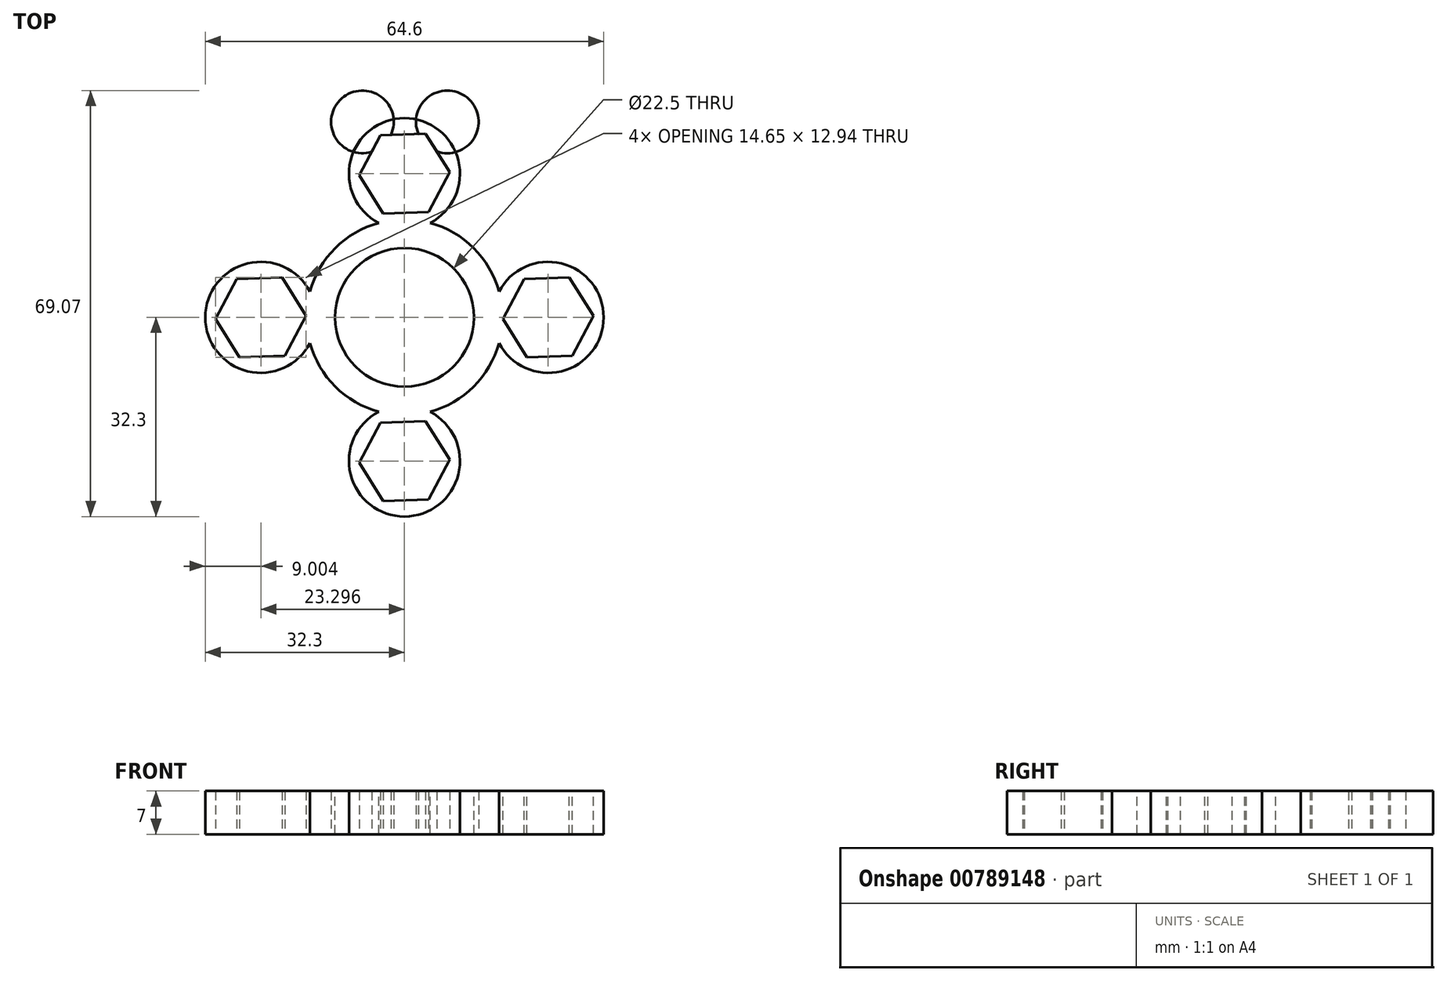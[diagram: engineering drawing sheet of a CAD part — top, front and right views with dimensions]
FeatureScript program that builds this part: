
annotation { "Feature Type Name" : "Feature", "Feature Type Description" : "" }
export const myFeature = defineFeature(function(context is Context, id is Id, definition is map)
    precondition{}
    {
        {
            var Q0;
            Q0=qCreatedBy(makeId("Top.planeOp"),FACE);
            var sketch = newSketch(context, id + "F0", { "sketchPlane" : qUnion([Q0])});
            skCircle(sketch, "E0", {"center": v(0, 0) * mm, "radius": 11.25 * mm});
            skSolve(sketch);
        }
        {
            var Q0;
            Q0=makeQuery(id+"F0.imprint","IMPRINT",FACE,{"disambiguationData":[TD([[makeQuery(id+"F0.imprint","IMPRINT",EDGE,{"derivedFrom":sQuery(id+"F0.wireOp",EDGE,"E0")}),1.0]])]});
            var sketch = newSketch(context, id + "F1", { "sketchPlane" : qUnion([Q0])});
            skCircle(sketch, "E1", {"center": v(0, 0) * mm, "radius": 14.3 * mm});
            skSolve(sketch);
        }
        {
            var Q0;
            Q0=makeQuery(id+"F0.imprint","IMPRINT",FACE,{"disambiguationData":[TD([[makeQuery(id+"F0.imprint","IMPRINT",EDGE,{"derivedFrom":sQuery(id+"F0.wireOp",EDGE,"E0")}),1.0]])]});
            var sketch = newSketch(context, id + "F2", { "sketchPlane" : qUnion([Q0])});
            skLineSegment(sketch, "E2", {"start": v(0, 0) * mm, "end": v(0, 55.77) * mm});
            skLineSegment(sketch, "E3", {"start": v(0, 55.77) * mm, "end": v(0, -44.4) * mm});
            skSolve(sketch);
        }
        {
            var Q0;
            Q0=makeQuery(id+"F0.imprint","IMPRINT",FACE,{"disambiguationData":[TD([[makeQuery(id+"F0.imprint","IMPRINT",EDGE,{"derivedFrom":sQuery(id+"F0.wireOp",EDGE,"E0")}),1.0]])]});
            var sketch = newSketch(context, id + "F3", { "sketchPlane" : qUnion([Q0])});
            skLineSegment(sketch, "E4", {"start": v(0, 0) * mm, "end": v(-73.88, 0) * mm});
            skLineSegment(sketch, "E5", {"start": v(-73.88, 0) * mm, "end": v(73.58, 0) * mm});
            skSolve(sketch);
        }
        {
            var Q0;
            Q0=makeQuery(id+"F0.imprint","IMPRINT",FACE,{"disambiguationData":[TD([[makeQuery(id+"F0.imprint","IMPRINT",EDGE,{"derivedFrom":sQuery(id+"F0.wireOp",EDGE,"E0")}),1.0]])]});
            var sketch = newSketch(context, id + "F4", { "sketchPlane" : qUnion([Q0])});
            skCircle(sketch, "E6", {"center": v(0, 23.3) * mm, "radius": 9 * mm});
            skSolve(sketch);
        }
        {
            var Q0;
            Q0=makeQuery(id+"F0.imprint","IMPRINT",FACE,{"disambiguationData":[TD([[makeQuery(id+"F0.imprint","IMPRINT",EDGE,{"derivedFrom":sQuery(id+"F0.wireOp",EDGE,"E0")}),1.0]])]});
            var sketch = newSketch(context, id + "F5", { "sketchPlane" : qUnion([Q0])});
            skCircle(sketch, "E7", {"center": v(-23.3, 0) * mm, "radius": 9 * mm});
            skSolve(sketch);
        }
        {
            var Q0;
            Q0=makeQuery(id+"F0.imprint","IMPRINT",FACE,{"disambiguationData":[TD([[makeQuery(id+"F0.imprint","IMPRINT",EDGE,{"derivedFrom":sQuery(id+"F0.wireOp",EDGE,"E0")}),1.0]])]});
            var sketch = newSketch(context, id + "F6", { "sketchPlane" : qUnion([Q0])});
            skCircle(sketch, "E8", {"center": v(0, -23.3) * mm, "radius": 9 * mm});
            skSolve(sketch);
        }
        {
            var Q0;
            Q0=makeQuery(id+"F0.imprint","IMPRINT",FACE,{"disambiguationData":[TD([[makeQuery(id+"F0.imprint","IMPRINT",EDGE,{"derivedFrom":sQuery(id+"F0.wireOp",EDGE,"E0")}),1.0]])]});
            var sketch = newSketch(context, id + "F7", { "sketchPlane" : qUnion([Q0])});
            skCircle(sketch, "E9", {"center": v(23.3, 0) * mm, "radius": 9 * mm});
            skSolve(sketch);
        }
        {
            var Q0;
            Q0=makeQuery(id+"F0.imprint","IMPRINT",FACE,{"disambiguationData":[TD([[makeQuery(id+"F0.imprint","IMPRINT",EDGE,{"derivedFrom":sQuery(id+"F0.wireOp",EDGE,"E0")}),1.0]])]});
            var sketch = newSketch(context, id + "F8", { "sketchPlane" : qUnion([Q0])});
            skCircle(sketch, "E10.cCircle", {"center": v(23.3, 0) * mm, "radius": 7.33 * mm, "construction": true});
            skLineSegment(sketch, "E10.0", {"start": v(26.73, 6.47) * mm, "end": v(30.62, 0.26) * mm});
            skLineSegment(sketch, "E10.1", {"start": v(30.62, 0.26) * mm, "end": v(27.18, -6.21) * mm});
            skLineSegment(sketch, "E10.2", {"start": v(27.18, -6.21) * mm, "end": v(19.86, -6.47) * mm});
            skLineSegment(sketch, "E10.3", {"start": v(19.86, -6.47) * mm, "end": v(15.97, -0.26) * mm});
            skLineSegment(sketch, "E10.4", {"start": v(15.97, -0.26) * mm, "end": v(19.4, 6.21) * mm});
            skLineSegment(sketch, "E10.5", {"start": v(19.4, 6.21) * mm, "end": v(26.73, 6.47) * mm});
            skSolve(sketch);
        }
        {
            var Q0;
            Q0=makeQuery(id+"F8.imprint","IMPRINT",FACE,{"disambiguationData":[TD([[makeQuery(id+"F8.imprint","IMPRINT",EDGE,{"derivedFrom":sQuery(id+"F8.wireOp",EDGE,"E10.0")}),-1.0]])]});
            var sketch = newSketch(context, id + "F9", { "sketchPlane" : qUnion([Q0])});
            skCircle(sketch, "E11.cCircle", {"center": v(0, -23.3) * mm, "radius": 7.33 * mm, "construction": true});
            skLineSegment(sketch, "E11.0", {"start": v(3.44, -16.82) * mm, "end": v(7.32, -23.04) * mm});
            skLineSegment(sketch, "E11.1", {"start": v(7.32, -23.04) * mm, "end": v(3.89, -29.5) * mm});
            skLineSegment(sketch, "E11.2", {"start": v(3.89, -29.5) * mm, "end": v(-3.44, -29.77) * mm});
            skLineSegment(sketch, "E11.3", {"start": v(-3.44, -29.77) * mm, "end": v(-7.32, -23.56) * mm});
            skLineSegment(sketch, "E11.4", {"start": v(-7.32, -23.56) * mm, "end": v(-3.89, -17.08) * mm});
            skLineSegment(sketch, "E11.5", {"start": v(-3.89, -17.08) * mm, "end": v(3.44, -16.82) * mm});
            skSolve(sketch);
        }
        {
            var Q0;
            Q0=makeQuery(id+"F5.imprint","IMPRINT",FACE,{"disambiguationData":[TD([[makeQuery(id+"F5.imprint","IMPRINT",EDGE,{"derivedFrom":sQuery(id+"F5.wireOp",EDGE,"E7")}),1.0]])]});
            var sketch = newSketch(context, id + "F10", { "sketchPlane" : qUnion([Q0])});
            skCircle(sketch, "E12.cCircle", {"center": v(-23.3, 0) * mm, "radius": 7.33 * mm, "construction": true});
            skLineSegment(sketch, "E12.0", {"start": v(-19.86, 6.47) * mm, "end": v(-15.97, 0.26) * mm});
            skLineSegment(sketch, "E12.1", {"start": v(-15.97, 0.26) * mm, "end": v(-19.4, -6.21) * mm});
            skLineSegment(sketch, "E12.2", {"start": v(-19.4, -6.21) * mm, "end": v(-26.73, -6.47) * mm});
            skLineSegment(sketch, "E12.3", {"start": v(-26.73, -6.47) * mm, "end": v(-30.62, -0.26) * mm});
            skLineSegment(sketch, "E12.4", {"start": v(-30.62, -0.26) * mm, "end": v(-27.18, 6.21) * mm});
            skLineSegment(sketch, "E12.5", {"start": v(-27.18, 6.21) * mm, "end": v(-19.86, 6.47) * mm});
            skSolve(sketch);
        }
        {
            var Q0;
            Q0=makeQuery(id+"F4.imprint","IMPRINT",FACE,{"disambiguationData":[TD([[makeQuery(id+"F4.imprint","IMPRINT",EDGE,{"derivedFrom":sQuery(id+"F4.wireOp",EDGE,"E6")}),1.0]])]});
            var sketch = newSketch(context, id + "F11", { "sketchPlane" : qUnion([Q0])});
            skCircle(sketch, "E13.cCircle", {"center": v(0, 23.3) * mm, "radius": 7.33 * mm, "construction": true});
            skLineSegment(sketch, "E13.0", {"start": v(3.44, 29.77) * mm, "end": v(7.32, 23.56) * mm});
            skLineSegment(sketch, "E13.1", {"start": v(7.32, 23.56) * mm, "end": v(3.89, 17.08) * mm});
            skLineSegment(sketch, "E13.2", {"start": v(3.89, 17.08) * mm, "end": v(-3.44, 16.82) * mm});
            skLineSegment(sketch, "E13.3", {"start": v(-3.44, 16.82) * mm, "end": v(-7.32, 23.04) * mm});
            skLineSegment(sketch, "E13.4", {"start": v(-7.32, 23.04) * mm, "end": v(-3.89, 29.5) * mm});
            skLineSegment(sketch, "E13.5", {"start": v(-3.89, 29.5) * mm, "end": v(3.44, 29.77) * mm});
            skSolve(sketch);
        }
        {
            var Q0;
            Q0=makeQuery(id+"F4.imprint","IMPRINT",FACE,{"disambiguationData":[TD([[makeQuery(id+"F4.imprint","IMPRINT",EDGE,{"derivedFrom":sQuery(id+"F4.wireOp",EDGE,"E6")}),1.0]])]});
            var sketch = newSketch(context, id + "F12", { "sketchPlane" : qUnion([Q0])});
            skCircle(sketch, "E14", {"center": v(-6.82, 31.69) * mm, "radius": 5.08 * mm});
            skCircle(sketch, "E15", {"center": v(6.94, 31.69) * mm, "radius": 5.08 * mm});
            skSolve(sketch);
        }
        {
            var Q0;
            Q0=makeQuery(id+"F1.imprint","IMPRINT",FACE,{"disambiguationData":[TD([[makeQuery(id+"F1.imprint","IMPRINT",EDGE,{"derivedFrom":makeQuery(id+"F0.imprint","IMPRINT",EDGE,{"derivedFrom":sQuery(id+"F0.wireOp",EDGE,"E0")})}),1.0]])]});
            var Q1;
            Q1=makeQuery(id+"F1.imprint","IMPRINT",FACE,{"disambiguationData":[TD([[makeQuery(id+"F1.imprint","IMPRINT",EDGE,{"derivedFrom":sQuery(id+"F1.wireOp",EDGE,"E1")}),1.0]])]});
            var Q2;
            {var subQ0=sQuery(id+"F2.wireOp",EDGE,"E3");var subQ1=makeQuery(id+"F2.imprint","IMPRINT",VERTEX,{"derivedFrom":subQ0});Q2=makeQuery(id+"F2.imprint","IMPRINT",FACE,{"disambiguationData":[TD([[makeQuery(id+"F2.imprint","IMPRINT",EDGE,{"disambiguationData":[TD([[subQ1,1.0]])],"derivedFrom":subQ0}),-1.0]])]});}
            var Q3;
            {var subQ0=sQuery(id+"F2.wireOp",EDGE,"E3");var subQ1=makeQuery(id+"F2.imprint","IMPRINT",VERTEX,{"derivedFrom":subQ0});Q3=makeQuery(id+"F2.imprint","IMPRINT",FACE,{"disambiguationData":[TD([[makeQuery(id+"F2.imprint","IMPRINT",EDGE,{"disambiguationData":[TD([[subQ1,1.0]])],"derivedFrom":subQ0}),1.0]])]});}
            var Q4;
            {var subQ0=sQuery(id+"F3.wireOp",EDGE,"E5");var subQ1=makeQuery(id+"F3.imprint","IMPRINT",VERTEX,{"derivedFrom":subQ0});Q4=makeQuery(id+"F3.imprint","IMPRINT",FACE,{"disambiguationData":[TD([[makeQuery(id+"F3.imprint","IMPRINT",EDGE,{"disambiguationData":[TD([[subQ1,1.0]])],"derivedFrom":subQ0}),-1.0]])]});}
            var Q5;
            {var subQ0=sQuery(id+"F3.wireOp",EDGE,"E5");var subQ1=makeQuery(id+"F3.imprint","IMPRINT",VERTEX,{"derivedFrom":subQ0});Q5=makeQuery(id+"F3.imprint","IMPRINT",FACE,{"disambiguationData":[TD([[makeQuery(id+"F3.imprint","IMPRINT",EDGE,{"disambiguationData":[TD([[subQ1,1.0]])],"derivedFrom":subQ0}),1.0]])]});}
            var Q6;
            Q6=makeQuery(id+"F4.imprint","IMPRINT",FACE,{"disambiguationData":[TD([[makeQuery(id+"F4.imprint","IMPRINT",EDGE,{"derivedFrom":sQuery(id+"F4.wireOp",EDGE,"E6")}),1.0]])]});
            var Q7;
            Q7=makeQuery(id+"F7.imprint","IMPRINT",FACE,{"disambiguationData":[TD([[makeQuery(id+"F7.imprint","IMPRINT",EDGE,{"derivedFrom":sQuery(id+"F7.wireOp",EDGE,"E9")}),1.0]])]});
            var Q8;
            Q8=makeQuery(id+"F6.imprint","IMPRINT",FACE,{"disambiguationData":[TD([[makeQuery(id+"F6.imprint","IMPRINT",EDGE,{"derivedFrom":sQuery(id+"F6.wireOp",EDGE,"E8")}),1.0]])]});
            var Q9;
            Q9=makeQuery(id+"F5.imprint","IMPRINT",FACE,{"disambiguationData":[TD([[makeQuery(id+"F5.imprint","IMPRINT",EDGE,{"derivedFrom":sQuery(id+"F5.wireOp",EDGE,"E7")}),1.0]])]});
            var Q10;
            Q10=makeQuery(id+"F9.imprint","IMPRINT",FACE,{"disambiguationData":[TD([[makeQuery(id+"F9.imprint","IMPRINT",EDGE,{"derivedFrom":makeQuery(id+"F8.imprint","IMPRINT",EDGE,{"derivedFrom":sQuery(id+"F8.wireOp",EDGE,"E10.0")})}),-1.0]])]});
            var Q11;
            Q11=makeQuery(id+"F10.imprint","IMPRINT",FACE,{"disambiguationData":[TD([[makeQuery(id+"F10.imprint","IMPRINT",EDGE,{"derivedFrom":sQuery(id+"F10.wireOp",EDGE,"E12.0")}),1.0]])]});
            var Q12;
            Q12=makeQuery(id+"F11.imprint","IMPRINT",FACE,{"disambiguationData":[TD([[makeQuery(id+"F11.imprint","IMPRINT",EDGE,{"derivedFrom":sQuery(id+"F11.wireOp",EDGE,"E13.0")}),1.0]])]});
            var Q13;
            Q13=makeQuery(id+"F12.imprint","IMPRINT",FACE,{"disambiguationData":[TD([[makeQuery(id+"F12.imprint","IMPRINT",EDGE,{"derivedFrom":sQuery(id+"F12.wireOp",EDGE,"E14")}),1.0]])]});
            var Q14;
            Q14=makeQuery(id+"F12.imprint","IMPRINT",FACE,{"disambiguationData":[TD([[makeQuery(id+"F12.imprint","IMPRINT",EDGE,{"derivedFrom":sQuery(id+"F12.wireOp",EDGE,"E15")}),1.0]])]});
            var Q15;
            Q15=makeQuery(id+"FDVSy74jOAvPm48_0.2.F12.imprint","IMPRINT",FACE,{"disambiguationData":[TD([[makeQuery(id+"FDVSy74jOAvPm48_0.2.F12.imprint","IMPRINT",EDGE,{"derivedFrom":sQuery(id+"FDVSy74jOAvPm48_0.2.F12.wireOp",EDGE,"E14")}),1.0]])]});
            var Q16;
            Q16=makeQuery(id+"FDVSy74jOAvPm48_0.-1.F12.imprint","IMPRINT",FACE,{"disambiguationData":[TD([[makeQuery(id+"FDVSy74jOAvPm48_0.-1.F12.imprint","IMPRINT",EDGE,{"derivedFrom":sQuery(id+"FDVSy74jOAvPm48_0.-1.F12.wireOp",EDGE,"E14")}),1.0]])]});
            var Q17;
            Q17=makeQuery(id+"FDVSy74jOAvPm48_0.2.F12.imprint","IMPRINT",FACE,{"disambiguationData":[TD([[makeQuery(id+"FDVSy74jOAvPm48_0.2.F12.imprint","IMPRINT",EDGE,{"derivedFrom":sQuery(id+"FDVSy74jOAvPm48_0.2.F12.wireOp",EDGE,"E15")}),1.0]])]});
            var Q18;
            Q18=makeQuery(id+"FDVSy74jOAvPm48_0.-1.F12.imprint","IMPRINT",FACE,{"disambiguationData":[TD([[makeQuery(id+"FDVSy74jOAvPm48_0.-1.F12.imprint","IMPRINT",EDGE,{"derivedFrom":sQuery(id+"FDVSy74jOAvPm48_0.-1.F12.wireOp",EDGE,"E15")}),1.0]])]});
            var Q19;
            Q19=makeQuery(id+"FDVSy74jOAvPm48_0.-3.F12.imprint","IMPRINT",FACE,{"disambiguationData":[TD([[makeQuery(id+"FDVSy74jOAvPm48_0.-3.F12.imprint","IMPRINT",EDGE,{"derivedFrom":sQuery(id+"FDVSy74jOAvPm48_0.-3.F12.wireOp",EDGE,"E14")}),1.0]])]});
            var Q20;
            Q20=makeQuery(id+"FDVSy74jOAvPm48_0.-3.F12.imprint","IMPRINT",FACE,{"disambiguationData":[TD([[makeQuery(id+"FDVSy74jOAvPm48_0.-3.F12.imprint","IMPRINT",EDGE,{"derivedFrom":sQuery(id+"FDVSy74jOAvPm48_0.-3.F12.wireOp",EDGE,"E15")}),1.0]])]});
            var Q21;
            Q21=makeQuery(id+"F4.imprint","IMPRINT",FACE,{"disambiguationData":[TD([[makeQuery(id+"F4.imprint","IMPRINT",EDGE,{"derivedFrom":makeQuery(id+"F0.imprint","IMPRINT",EDGE,{"derivedFrom":sQuery(id+"F0.wireOp",EDGE,"E0")})}),1.0]])]});
            var Q22;
            {var subQ0=makeQuery(id+"F4.imprint","IMPRINT",EDGE,{"derivedFrom":sQuery(id+"F4.wireOp",EDGE,"E6")});var subQ1=makeQuery(id+"F12.imprint","INTERSECT",VERTEX,{"derivedFrom":[subQ0,sQuery(id+"F12.wireOp",EDGE,"E14")]});Q22=makeQuery(id+"F12.imprint","IMPRINT",FACE,{"disambiguationData":[TD([[makeQuery(id+"F12.imprint","IMPRINT",EDGE,{"disambiguationData":[TD([[subQ1,-1.0]])],"derivedFrom":subQ0}),1.0]])]});}
            var Q23;
            Q23=makeQuery(id+"FDVSy74jOAvPm48_0.3.F12.imprint","IMPRINT",FACE,{"disambiguationData":[TD([[makeQuery(id+"FDVSy74jOAvPm48_0.3.F12.imprint","IMPRINT",EDGE,{"derivedFrom":sQuery(id+"FDVSy74jOAvPm48_0.3.F12.wireOp",EDGE,"E14")}),1.0]])]});
            var Q24;
            Q24=makeQuery(id+"FDVSy74jOAvPm48_0.3.F12.imprint","IMPRINT",FACE,{"disambiguationData":[TD([[makeQuery(id+"FDVSy74jOAvPm48_0.3.F12.imprint","IMPRINT",EDGE,{"derivedFrom":sQuery(id+"FDVSy74jOAvPm48_0.3.F12.wireOp",EDGE,"E15")}),1.0]])]});
            var Q25;
            Q25=makeQuery(id+"FDVSy74jOAvPm48_0.1.F12.imprint","IMPRINT",FACE,{"disambiguationData":[TD([[makeQuery(id+"FDVSy74jOAvPm48_0.1.F12.imprint","IMPRINT",EDGE,{"derivedFrom":sQuery(id+"FDVSy74jOAvPm48_0.1.F12.wireOp",EDGE,"E14")}),1.0]])]});
            var Q26;
            Q26=makeQuery(id+"FDVSy74jOAvPm48_0.-2.F12.imprint","IMPRINT",FACE,{"disambiguationData":[TD([[makeQuery(id+"FDVSy74jOAvPm48_0.-2.F12.imprint","IMPRINT",EDGE,{"derivedFrom":sQuery(id+"FDVSy74jOAvPm48_0.-2.F12.wireOp",EDGE,"E14")}),1.0]])]});
            var Q27;
            Q27=makeQuery(id+"FDVSy74jOAvPm48_0.1.F12.imprint","IMPRINT",FACE,{"disambiguationData":[TD([[makeQuery(id+"FDVSy74jOAvPm48_0.1.F12.imprint","IMPRINT",EDGE,{"derivedFrom":sQuery(id+"FDVSy74jOAvPm48_0.1.F12.wireOp",EDGE,"E15")}),1.0]])]});
            var Q28;
            Q28=makeQuery(id+"FDVSy74jOAvPm48_0.-2.F12.imprint","IMPRINT",FACE,{"disambiguationData":[TD([[makeQuery(id+"FDVSy74jOAvPm48_0.-2.F12.imprint","IMPRINT",EDGE,{"derivedFrom":sQuery(id+"FDVSy74jOAvPm48_0.-2.F12.wireOp",EDGE,"E15")}),1.0]])]});
            var Q29;
            Q29=makeQuery(id+"F5.imprint","IMPRINT",FACE,{"disambiguationData":[TD([[makeQuery(id+"F5.imprint","IMPRINT",EDGE,{"derivedFrom":makeQuery(id+"F0.imprint","IMPRINT",EDGE,{"derivedFrom":sQuery(id+"F0.wireOp",EDGE,"E0")})}),1.0]])]});
            var Q30;
            Q30=makeQuery(id+"F9.imprint","IMPRINT",FACE,{"disambiguationData":[TD([[makeQuery(id+"F9.imprint","IMPRINT",EDGE,{"derivedFrom":sQuery(id+"F9.wireOp",EDGE,"E11.0")}),-1.0]])]});
            var Q31;
            Q31=makeQuery(id+"F10.imprint","IMPRINT",FACE,{"disambiguationData":[TD([[makeQuery(id+"F10.imprint","IMPRINT",EDGE,{"derivedFrom":sQuery(id+"F10.wireOp",EDGE,"E12.0")}),-1.0]])]});
            var Q32;
            Q32=makeQuery(id+"F11.imprint","IMPRINT",FACE,{"disambiguationData":[TD([[makeQuery(id+"F11.imprint","IMPRINT",EDGE,{"derivedFrom":sQuery(id+"F11.wireOp",EDGE,"E13.0")}),-1.0]])]});
            var Q33;
            Q33=makeQuery(id+"F6.imprint","IMPRINT",FACE,{"disambiguationData":[TD([[makeQuery(id+"F6.imprint","IMPRINT",EDGE,{"derivedFrom":makeQuery(id+"F0.imprint","IMPRINT",EDGE,{"derivedFrom":sQuery(id+"F0.wireOp",EDGE,"E0")})}),1.0]])]});
            var Q34;
            Q34=makeQuery(id+"F7.imprint","IMPRINT",FACE,{"disambiguationData":[TD([[makeQuery(id+"F7.imprint","IMPRINT",EDGE,{"derivedFrom":makeQuery(id+"F0.imprint","IMPRINT",EDGE,{"derivedFrom":sQuery(id+"F0.wireOp",EDGE,"E0")})}),1.0]])]});
            extrude(context, id + "F13", {"entities" : qUnion([Q0, Q1, Q2, Q3, Q4, Q5, Q6, Q7, Q8, Q9, Q10, Q11, Q12, Q13, Q14, Q15, Q16, Q17, Q18, Q19, Q20, Q21, Q22, Q23, Q24, Q25, Q26, Q27, Q28, Q29, Q30, Q31, Q32, Q33, Q34]), "depth" : 7 * mm, "offsetDistance" : 25.4 * mm});
        }
        {
            var Q0;
            Q0=makeQuery(id+"F13.opExtrude","CAP_FACE",FACE,{"disambiguationData":[OSD([sQuery(id+"F8.wireOp",EDGE,"E10.0"),sQuery(id+"F8.wireOp",EDGE,"E10.1"),sQuery(id+"F8.wireOp",EDGE,"E10.2"),sQuery(id+"F8.wireOp",EDGE,"E10.3"),sQuery(id+"F8.wireOp",EDGE,"E10.4"),sQuery(id+"F8.wireOp",EDGE,"E10.5")])],"isStart":false});
            extrude(context, id + "F14", {"entities" : qUnion([Q0]), "operationType" : NewBodyOperationType.REMOVE, "endBound" : BoundingType.THROUGH_ALL, "oppositeDirection" : true, "depth" : 25.4 * mm, "offsetDistance" : 25.4 * mm});
        }
        {
            var Q0;
            Q0=makeQuery(id+"F13.opExtrude","CAP_FACE",FACE,{"disambiguationData":[OSD([sQuery(id+"F1.wireOp",EDGE,"E1")])],"isStart":false});
            var sketch = newSketch(context, id + "F15", { "sketchPlane" : qUnion([Q0])});
            skCircle(sketch, "E16", {"center": v(0, 0) * mm, "radius": 11.25 * mm});
            skSolve(sketch);
        }
        {
            var Q0;
            Q0=makeQuery(id+"F15.imprint","IMPRINT",FACE,{"disambiguationData":[TD([[makeQuery(id+"F15.imprint","IMPRINT",EDGE,{"derivedFrom":sQuery(id+"F15.wireOp",EDGE,"E16")}),1.0]])]});
            extrude(context, id + "F16", {"entities" : qUnion([Q0]), "operationType" : NewBodyOperationType.REMOVE, "endBound" : BoundingType.THROUGH_ALL, "oppositeDirection" : true, "depth" : 25.4 * mm, "offsetDistance" : 25.4 * mm});
        }
        {
            var Q0;
            Q0=makeQuery(id+"F13.opExtrude","CAP_FACE",FACE,{"disambiguationData":[OSD([sQuery(id+"F6.wireOp",EDGE,"E8")])],"isStart":false});
            var sketch = newSketch(context, id + "F17", { "sketchPlane" : qUnion([Q0])});
            skCircle(sketch, "E17.cCircle", {"center": v(0, -23.3) * mm, "radius": 3.97 * mm, "construction": true});
            skLineSegment(sketch, "E17.0", {"start": v(3.97, -23.18) * mm, "end": v(2.09, -26.67) * mm});
            skLineSegment(sketch, "E17.1", {"start": v(2.09, -26.67) * mm, "end": v(-1.88, -26.8) * mm});
            skLineSegment(sketch, "E17.2", {"start": v(-1.88, -26.8) * mm, "end": v(-3.97, -23.42) * mm});
            skLineSegment(sketch, "E17.3", {"start": v(-3.97, -23.42) * mm, "end": v(-2.09, -19.92) * mm});
            skLineSegment(sketch, "E17.4", {"start": v(-2.09, -19.92) * mm, "end": v(1.88, -19.8) * mm});
            skLineSegment(sketch, "E17.5", {"start": v(1.88, -19.8) * mm, "end": v(3.97, -23.18) * mm});
            skSolve(sketch);
        }
        {
            var Q0;
            Q0=makeQuery(id+"F17.imprint","IMPRINT",FACE,{"disambiguationData":[TD([[makeQuery(id+"F17.imprint","IMPRINT",EDGE,{"derivedFrom":sQuery(id+"F17.wireOp",EDGE,"E17.0")}),-1.0]])]});
            extrude(context, id + "F18", {"entities" : qUnion([Q0]), "operationType" : NewBodyOperationType.REMOVE, "endBound" : BoundingType.THROUGH_ALL, "oppositeDirection" : true, "depth" : 25.4 * mm, "offsetDistance" : 25.4 * mm});
        }
        {
            var Q0;
            {var subQ0=sQuery(id+"F5.wireOp",EDGE,"E7");Q0=makeQuery(id+"F13.opExtrude","CAP_FACE",FACE,{"disambiguationData":[OSD([subQ0]),TDD([makeQuery(id+"F5.imprint","IMPRINT",EDGE,{"derivedFrom":subQ0})])],"isStart":false});}
            var sketch = newSketch(context, id + "F19", { "sketchPlane" : qUnion([Q0])});
            skCircle(sketch, "E18.cCircle", {"center": v(-23.3, 0) * mm, "radius": 3.97 * mm, "construction": true});
            skLineSegment(sketch, "E18.0", {"start": v(-20.48, -2.8) * mm, "end": v(-24.3, -3.84) * mm});
            skLineSegment(sketch, "E18.1", {"start": v(-24.3, -3.84) * mm, "end": v(-27.13, -1.04) * mm});
            skLineSegment(sketch, "E18.2", {"start": v(-27.13, -1.04) * mm, "end": v(-26.11, 2.8) * mm});
            skLineSegment(sketch, "E18.3", {"start": v(-26.11, 2.8) * mm, "end": v(-22.28, 3.84) * mm});
            skLineSegment(sketch, "E18.4", {"start": v(-22.28, 3.84) * mm, "end": v(-19.47, 1.04) * mm});
            skLineSegment(sketch, "E18.5", {"start": v(-19.47, 1.04) * mm, "end": v(-20.48, -2.8) * mm});
            skSolve(sketch);
        }
        {
            var Q0;
            Q0=makeQuery(id+"F19.imprint","IMPRINT",FACE,{"disambiguationData":[TD([[makeQuery(id+"F19.imprint","IMPRINT",EDGE,{"derivedFrom":sQuery(id+"F19.wireOp",EDGE,"E18.0")}),-1.0]])]});
            extrude(context, id + "F20", {"entities" : qUnion([Q0]), "operationType" : NewBodyOperationType.REMOVE, "endBound" : BoundingType.THROUGH_ALL, "oppositeDirection" : true, "depth" : 25.4 * mm, "offsetDistance" : 25.4 * mm});
        }
        {
            var Q0;
            {var subQ0=sQuery(id+"F4.wireOp",EDGE,"E6");Q0=makeQuery(id+"F13.opExtrude","CAP_FACE",FACE,{"disambiguationData":[OSD([subQ0]),TDD([makeQuery(id+"F4.imprint","IMPRINT",EDGE,{"derivedFrom":subQ0})])],"isStart":false});}
            var sketch = newSketch(context, id + "F21", { "sketchPlane" : qUnion([Q0])});
            skCircle(sketch, "E19.cCircle", {"center": v(0, 23.3) * mm, "radius": 3.97 * mm, "construction": true});
            skLineSegment(sketch, "E19.0", {"start": v(3.04, 20.75) * mm, "end": v(-0.69, 19.39) * mm});
            skLineSegment(sketch, "E19.1", {"start": v(-0.69, 19.39) * mm, "end": v(-3.73, 21.94) * mm});
            skLineSegment(sketch, "E19.2", {"start": v(-3.73, 21.94) * mm, "end": v(-3.04, 25.85) * mm});
            skLineSegment(sketch, "E19.3", {"start": v(-3.04, 25.85) * mm, "end": v(0.69, 27.2) * mm});
            skLineSegment(sketch, "E19.4", {"start": v(0.69, 27.2) * mm, "end": v(3.73, 24.65) * mm});
            skLineSegment(sketch, "E19.5", {"start": v(3.73, 24.65) * mm, "end": v(3.04, 20.75) * mm});
            skSolve(sketch);
        }
        {
            var Q0;
            Q0=makeQuery(id+"F21.imprint","IMPRINT",FACE,{"disambiguationData":[TD([[makeQuery(id+"F21.imprint","IMPRINT",EDGE,{"derivedFrom":sQuery(id+"F21.wireOp",EDGE,"E19.0")}),-1.0]])]});
            extrude(context, id + "F22", {"entities" : qUnion([Q0]), "operationType" : NewBodyOperationType.REMOVE, "endBound" : BoundingType.THROUGH_ALL, "oppositeDirection" : true, "depth" : 25.4 * mm, "offsetDistance" : 25.4 * mm});
        }
        {
            var Q0;
            Q0=makeQuery(id+"F13.opExtrude","CAP_FACE",FACE,{"disambiguationData":[OSD([sQuery(id+"F1.wireOp",EDGE,"E1")])],"isStart":false});
            var sketch = newSketch(context, id + "F23", { "sketchPlane" : qUnion([Q0])});
            skCircle(sketch, "E20", {"center": v(0, 0) * mm, "radius": 15.87 * mm});
            skSolve(sketch);
        }
        {
            var Q0;
            Q0=makeQuery(id+"F23.imprint","IMPRINT",FACE,{"disambiguationData":[TD([[makeQuery(id+"F23.imprint","IMPRINT",EDGE,{"derivedFrom":sQuery(id+"F23.wireOp",EDGE,"E20")}),1.0]])]});
            var Q1;
            Q1=sQuery(id+"F23.wireOp",EDGE,"E20");
            var Q2;
            Q2=makeQuery(id+"F13.opExtrude","CAP_FACE",FACE,{"disambiguationData":[OSD([sQuery(id+"F1.wireOp",EDGE,"E1")])],"isStart":true});
            extrude(context, id + "F24", {"entities" : qUnion([Q0]), "operationType" : NewBodyOperationType.ADD, "surfaceEntities" : qUnion([Q1]), "endBound" : BoundingType.UP_TO_SURFACE, "oppositeDirection" : true, "depth" : 25.4 * mm, "endBoundEntityFace" : qUnion([Q2]), "offsetDistance" : 25.4 * mm});
        }
        {
            var Q0;
            Q0 = qSketchRegion(id + "F9", true);
            extrude(context, id + "F25", {"entities" : qUnion([Q0]), "operationType" : NewBodyOperationType.REMOVE, "endBound" : BoundingType.THROUGH_ALL, "depth" : 25.4 * mm, "offsetDistance" : 25.4 * mm});
        }
        {
            var Q0;
            Q0=makeQuery(id+"F8.imprint","IMPRINT",FACE,{"disambiguationData":[TD([[makeQuery(id+"F8.imprint","IMPRINT",EDGE,{"derivedFrom":sQuery(id+"F8.wireOp",EDGE,"E10.0")}),-1.0]])]});
            extrude(context, id + "F26", {"entities" : qUnion([Q0]), "operationType" : NewBodyOperationType.REMOVE, "endBound" : BoundingType.THROUGH_ALL, "depth" : 25.4 * mm, "offsetDistance" : 25.4 * mm});
        }
        {
            var Q0;
            Q0 = qSketchRegion(id + "F10", true);
            extrude(context, id + "F27", {"entities" : qUnion([Q0]), "operationType" : NewBodyOperationType.REMOVE, "endBound" : BoundingType.THROUGH_ALL, "depth" : 25.4 * mm, "offsetDistance" : 25.4 * mm});
        }
        {
            var Q0;
            Q0 = qSketchRegion(id + "F11", true);
            extrude(context, id + "F28", {"entities" : qUnion([Q0]), "operationType" : NewBodyOperationType.REMOVE, "endBound" : BoundingType.THROUGH_ALL, "depth" : 25.4 * mm, "offsetDistance" : 25.4 * mm});
        }
    });
